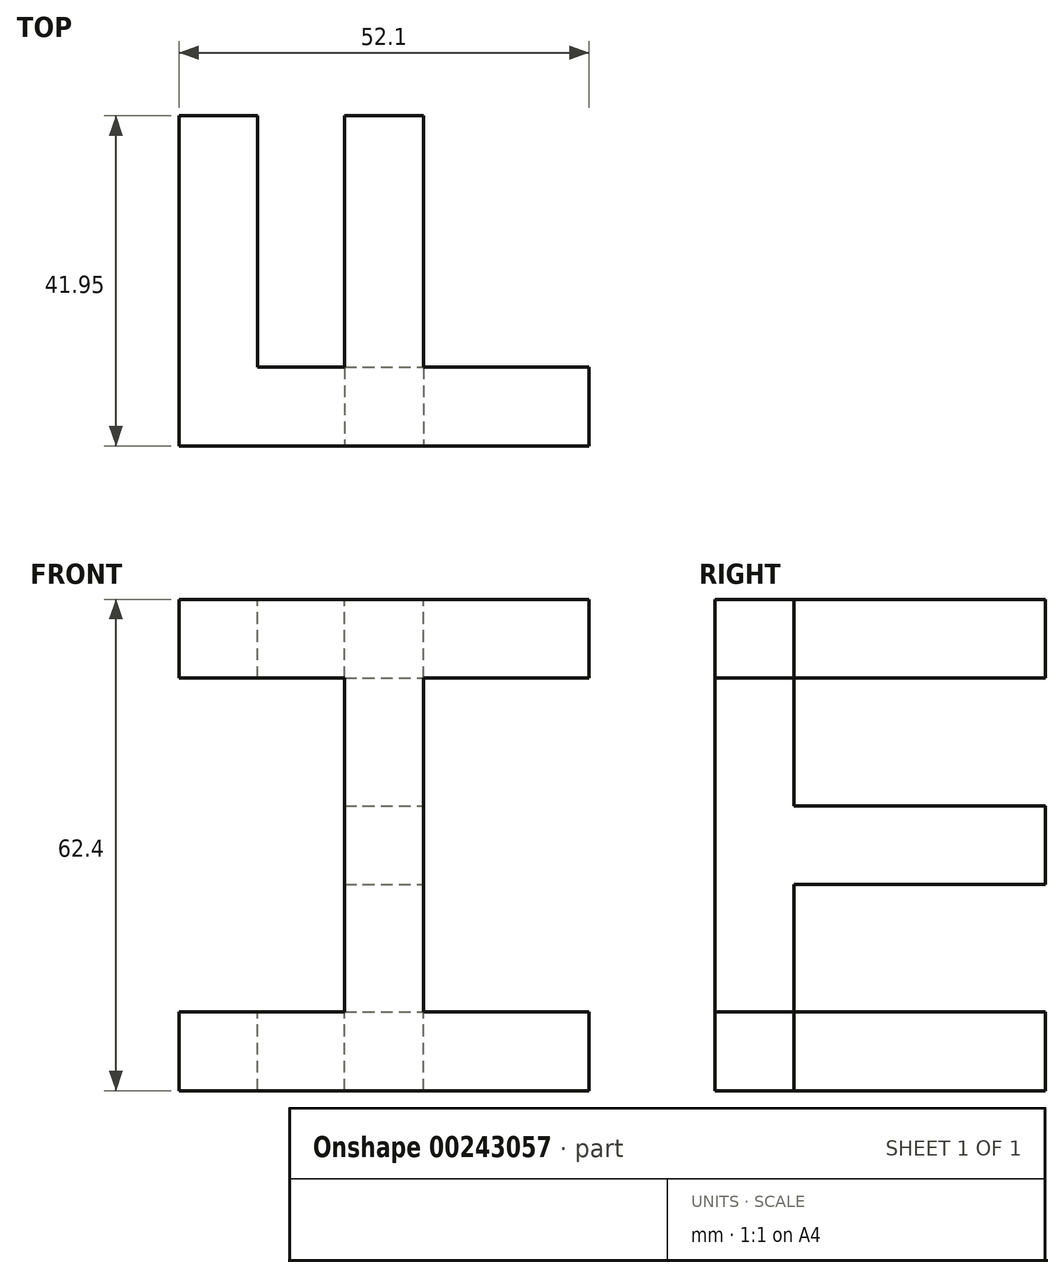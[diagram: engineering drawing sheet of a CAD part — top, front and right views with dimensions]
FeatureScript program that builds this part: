
annotation { "Feature Type Name" : "Feature", "Feature Type Description" : "" }
export const myFeature = defineFeature(function(context is Context, id is Id, definition is map)
    precondition{}
    {
        {
            var Q0;
            Q0=qCreatedBy(makeId("Top.planeOp"),FACE);
            var sketch = newSketch(context, id + "F0", { "sketchPlane" : qUnion([Q0])});
            skLineSegment(sketch, "E0.bottom", {"start": v(0, 0) * mm, "end": v(41.95, 0) * mm});
            skLineSegment(sketch, "E0.top", {"start": v(0, 62.4) * mm, "end": v(41.95, 62.4) * mm});
            skLineSegment(sketch, "E0.left", {"start": v(0, 0) * mm, "end": v(0, 62.4) * mm});
            skLineSegment(sketch, "E0.right", {"start": v(41.95, 0) * mm, "end": v(41.95, 62.4) * mm});
            skSolve(sketch);
        }
        {
            var Q0;
            Q0 = qSketchRegion(id + "F0", true);
            extrude(context, id + "F1", {"entities" : qUnion([Q0]), "depth" : 52.1 * mm});
        }
        {
            var Q0;
            Q0=makeQuery(id+"F1.opExtrude","CAP_FACE",FACE,{"disambiguationData":[OSD([sQuery(id+"F0.wireOp",EDGE,"E0.bottom"),sQuery(id+"F0.wireOp",EDGE,"E0.top"),sQuery(id+"F0.wireOp",EDGE,"E0.left"),sQuery(id+"F0.wireOp",EDGE,"E0.right")])],"isStart":false});
            var sketch = newSketch(context, id + "F2", { "sketchPlane" : qUnion([Q0])});
            skLineSegment(sketch, "E1.bottom", {"start": v(10, 36.2) * mm, "end": v(41.95, 36.2) * mm});
            skLineSegment(sketch, "E1.top", {"start": v(10, 52.4) * mm, "end": v(41.95, 52.4) * mm});
            skLineSegment(sketch, "E1.left", {"start": v(10, 36.2) * mm, "end": v(10, 52.4) * mm});
            skLineSegment(sketch, "E1.right", {"start": v(41.95, 36.2) * mm, "end": v(41.95, 52.4) * mm});
            skLineSegment(sketch, "E2.bottom", {"start": v(10, 26.2) * mm, "end": v(41.95, 26.2) * mm});
            skLineSegment(sketch, "E2.top", {"start": v(10, 10) * mm, "end": v(41.95, 10) * mm});
            skLineSegment(sketch, "E2.left", {"start": v(10, 26.2) * mm, "end": v(10, 10) * mm});
            skLineSegment(sketch, "E2.right", {"start": v(41.95, 26.2) * mm, "end": v(41.95, 10) * mm});
            skSolve(sketch);
        }
        {
            var Q0;
            Q0 = qSketchRegion(id + "F2", true);
            extrude(context, id + "F3", {"entities" : qUnion([Q0]), "operationType" : NewBodyOperationType.REMOVE, "oppositeDirection" : true, "depth" : 100 * mm});
        }
        {
            var Q0;
            Q0=makeQuery(id+"F1.opExtrude","SWEPT_FACE",FACE,{"disambiguationData":[OSD([sQuery(id+"F0.wireOp",EDGE,"E0.top")])]});
            var sketch = newSketch(context, id + "F4", { "sketchPlane" : qUnion([Q0])});
            skLineSegment(sketch, "E3.bottom", {"start": v(-10, 10) * mm, "end": v(-41.95, 10) * mm});
            skLineSegment(sketch, "E3.top", {"start": v(-10, 21.05) * mm, "end": v(-41.95, 21.05) * mm});
            skLineSegment(sketch, "E3.left", {"start": v(-10, 10) * mm, "end": v(-10, 21.05) * mm});
            skLineSegment(sketch, "E3.right", {"start": v(-41.95, 10) * mm, "end": v(-41.95, 21.05) * mm});
            skLineSegment(sketch, "E4.bottom", {"start": v(-10, 31.05) * mm, "end": v(-41.95, 31.05) * mm});
            skLineSegment(sketch, "E4.top", {"start": v(-10, 42.1) * mm, "end": v(-41.95, 42.1) * mm});
            skLineSegment(sketch, "E4.left", {"start": v(-10, 31.05) * mm, "end": v(-10, 42.1) * mm});
            skLineSegment(sketch, "E4.right", {"start": v(-41.95, 31.05) * mm, "end": v(-41.95, 42.1) * mm});
            skLineSegment(sketch, "E5.bottom", {"start": v(-10, 31.05) * mm, "end": v(-99.85, 31.05) * mm});
            skLineSegment(sketch, "E5.top", {"start": v(-10, 116.68) * mm, "end": v(-99.85, 116.68) * mm});
            skLineSegment(sketch, "E5.left", {"start": v(-10, 31.05) * mm, "end": v(-10, 116.68) * mm});
            skLineSegment(sketch, "E5.right", {"start": v(-99.85, 31.05) * mm, "end": v(-99.85, 116.68) * mm});
            skSolve(sketch);
        }
        {
            var Q0;
            Q0 = qSketchRegion(id + "F4", true);
            extrude(context, id + "F5", {"entities" : qUnion([Q0]), "operationType" : NewBodyOperationType.REMOVE, "oppositeDirection" : true, "depth" : 100 * mm});
        }
        {
            var Q0;
            Q0=makeQuery(id+"F1.opExtrude","SWEPT_FACE",FACE,{"disambiguationData":[OSD([sQuery(id+"F0.wireOp",EDGE,"E0.left")])]});
            var sketch = newSketch(context, id + "F6", { "sketchPlane" : qUnion([Q0])});
            skLineSegment(sketch, "E6.bottom", {"start": v(-52.4, 52.1) * mm, "end": v(-10, 52.1) * mm});
            skLineSegment(sketch, "E6.top", {"start": v(-52.4, 31.05) * mm, "end": v(-10, 31.05) * mm});
            skLineSegment(sketch, "E6.left", {"start": v(-52.4, 52.1) * mm, "end": v(-52.4, 31.05) * mm});
            skLineSegment(sketch, "E6.right", {"start": v(-10, 52.1) * mm, "end": v(-10, 31.05) * mm});
            skLineSegment(sketch, "E7.bottom", {"start": v(-52.4, 21.05) * mm, "end": v(-10, 21.05) * mm});
            skLineSegment(sketch, "E7.top", {"start": v(-52.4, 0) * mm, "end": v(-10, 0) * mm});
            skLineSegment(sketch, "E7.left", {"start": v(-52.4, 21.05) * mm, "end": v(-52.4, 0) * mm});
            skLineSegment(sketch, "E7.right", {"start": v(-10, 21.05) * mm, "end": v(-10, 0) * mm});
            skSolve(sketch);
        }
        {
            var Q0;
            Q0 = qSketchRegion(id + "F6", true);
            extrude(context, id + "F7", {"entities" : qUnion([Q0]), "operationType" : NewBodyOperationType.REMOVE, "oppositeDirection" : true, "depth" : 100 * mm});
        }
        {
            var Q0;
            Q0=makeQuery(id+"F1.opExtrude","SWEPT_BODY",BODY,{"disambiguationData":[OSD([sQuery(id+"F0.wireOp",EDGE,"E0.bottom"),sQuery(id+"F0.wireOp",EDGE,"E0.top"),sQuery(id+"F0.wireOp",EDGE,"E0.left"),sQuery(id+"F0.wireOp",EDGE,"E0.right")])]});
            var Q1;
            Q1=makeQuery(id+"F1.opExtrude","SWEPT_EDGE",EDGE,{"disambiguationData":[OSD([sQuery(id+"F0.wireOp",EDGE,"E0.bottom"),sQuery(id+"F0.wireOp",EDGE,"E0.left")])]});
            transform(context, id + "F8", {"entities" : qUnion([Q0]), "transformType" : TransformType.ROTATION, "transformAxis" : qUnion([Q1]), "angle" : 180 * degree, "makeCopy" : false});
        }
        {
            var Q0;
            Q0=makeQuery(id+"F1.opExtrude","SWEPT_BODY",BODY,{"disambiguationData":[OSD([sQuery(id+"F0.wireOp",EDGE,"E0.bottom"),sQuery(id+"F0.wireOp",EDGE,"E0.top"),sQuery(id+"F0.wireOp",EDGE,"E0.left"),sQuery(id+"F0.wireOp",EDGE,"E0.right")])]});
            var Q1;
            {var subQ0=sQuery(id+"F0.wireOp",EDGE,"E0.left");Q1=makeQuery(id+"F7.boolean.opBoolean","MERGE",EDGE,{"derivedFrom":[makeQuery(id+"F3.boolean.opBoolean","INTERSECT",EDGE,{"derivedFrom":[makeQuery(id+"F1.opExtrude","CAP_FACE",FACE,{"disambiguationData":[OSD([sQuery(id+"F0.wireOp",EDGE,"E0.bottom"),sQuery(id+"F0.wireOp",EDGE,"E0.top"),subQ0,sQuery(id+"F0.wireOp",EDGE,"E0.right")])],"isStart":true}),makeQuery(id+"F3.opExtrude","SWEPT_FACE",FACE,{"disambiguationData":[OSD([sQuery(id+"F2.wireOp",EDGE,"E2.top")])]})]}),makeQuery(id+"F7.opExtrude","SWEPT_EDGE",EDGE,{"disambiguationData":[OSD([subQ0,sQuery(id+"F6.wireOp",EDGE,"E7.top"),sQuery(id+"F6.wireOp",EDGE,"E7.right")])]})]});}
            transform(context, id + "F9", {"entities" : qUnion([Q0]), "transformType" : TransformType.ROTATION, "transformAxis" : qUnion([Q1]), "angle" : 90 * degree, "makeCopy" : false});
        }
        {
            var Q0;
            Q0=makeQuery(id+"F1.opExtrude","SWEPT_BODY",BODY,{"disambiguationData":[OSD([sQuery(id+"F0.wireOp",EDGE,"E0.bottom"),sQuery(id+"F0.wireOp",EDGE,"E0.top"),sQuery(id+"F0.wireOp",EDGE,"E0.left"),sQuery(id+"F0.wireOp",EDGE,"E0.right")])]});
            var Q1;
            {var subQ0=sQuery(id+"F0.wireOp",EDGE,"E0.left");var subQ1=sQuery(id+"F0.wireOp",EDGE,"E0.bottom");Q1=makeQuery(id+"F7.boolean.opBoolean","SPLIT",EDGE,{"disambiguationData":[TD([makeQuery(id+"F1.opExtrude","SWEPT_FACE",FACE,{"disambiguationData":[OSD([subQ1])]})])],"derivedFrom":makeQuery(id+"F1.opExtrude","CAP_EDGE",EDGE,{"disambiguationData":[OSD([subQ0])],"isStart":true})});}
            transform(context, id + "F10", {"entities" : qUnion([Q0]), "transformType" : TransformType.ROTATION, "transformAxis" : qUnion([Q1]), "angle" : 90 * degree, "oppositeDirection" : true, "makeCopy" : false});
        }
    });
